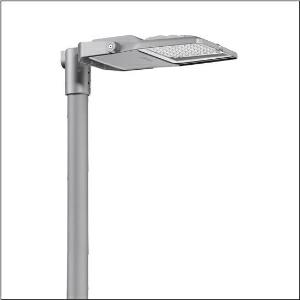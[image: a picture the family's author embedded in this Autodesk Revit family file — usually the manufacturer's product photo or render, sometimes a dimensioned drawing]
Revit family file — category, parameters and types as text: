
# Revit family: floodlight_fl_21_iq_mini___pl64_5xa7772b4e3a_29df
name_source: partatom
category: Lighting Fixtures
units: mm (PartAtom-declared; Revit-internal decimal feet)

## family parameters
Cut with Voids When Loaded = No
Host = Face
Light Source = No
Part Type = Normal
Room Calculation Point = No
Round Connector Dimension = Use Diameter
Shared = No

## types (1)
- --- (1 x LED, 6270 lm, 45.5 W, 4000K)
    Apparent Load = 46 VA
    CIE Flux Codes = 28 80 98 100 100
    Color Rendering = 70
    Color Temperature = 4000K
    Default Elevation = 1800 mm
    Description = Floodlight FL 21 iQ mini, floodlight, primary light control with lens, of PMMA, primary optical cover: protective disc, of toughened safety glass, transparent, light distribution: PL64, light emission: direct distribution, installation type: surface-mounted, LED, High Power LED, rated luminous flux: 6.270lm, luminous efficacy: 138lm/W, light colour: 740, colour temperature: 4000K, control: Auto-Match, Temp-Guard, Night-Set, Smart-Wire, Desk-Remote (wireless, voltage-free reading and setting of iQ features in the workshop via application-optimized NFC function/RFID function), optimised constant luminous flux control (CLO 2.0), Light-Fading, Lumen-Switch, with terminal, 6-pole, mains connection: 220..240V, AC, 50/60Hz, start of lifetime: 46W, end of service life: 48W, reduction: 22W, luminaire housing, of diecast aluminium, powder-coated, Siteco® metallic grey (DB 702S), corrosivity category C5 mid according to DIN EN ISO 12944, sealing non-destructively replaceable, please order mast flange separately, mast bracket, of steel, galvanised, powder-coated, protection rating (complete): IP66, insulation class (complete): insulation class II (safety insulation), certification: CE, ENEC, VDE, protection symbol: D, impact resistance: IK08, permissible operating ambient temperature: -40..+40°C, permissible operating ambient temperature for outdoor applications: -40..+50°C, standard: DIN EN 12944, LABS conformity tested according to VDMA 24364:2018-05, packaging unit: 1 piece

Light Distribution: PL64
    Height = 70 mm
    Lamp = 1 x LED
    Lamp Light Flux = 6270 lm
    Lamp Power = 45.5 W
    Lamp count = 1
    Length = 485 mm
    Luminous efficacy = 138 lm/W
    Manufacturer = Siteco
    ModVariant = No
    Model = 5XA7772B4E3A
    Number of Poles = 1
    OnlyDefault = Yes
    Power Factor = 1
    Product Name = Floodlight FL 21 iQ mini | PL64
    Product group = floodlight | pylon annexe
    ProductGroupID = 6200
    Protection Class = Protection class II
    Protection Degree = IP 66
    RLX_Detail_Level = 1
    RLX_Emergency_Light_Flux = 0 lm
    RLX_Emergency_Type = 0
    RLX_Emergency_Type_DB = No
    RlxData = <blob elided: 101133 chars, md5=ccd89305>
    Socket = socket
    Standby Power = 0 W
    System Light Flux = 6270 lm
    System Power = 46 W
    Type Comments = factory setting: luminous flux: 100 % | dim-lin: 254 | 463 mA
    Type Image = l_1007125.jpg
    URL = http://relux.com
    VarID = @adj_137091
    Voltage = 0 V
    Weight = 0.00 kg
    Width = 337 mm

## geometry (parser evidence)
native form markers: Blend x4, Sweep x12
no freeform markers — native parametric forms only
